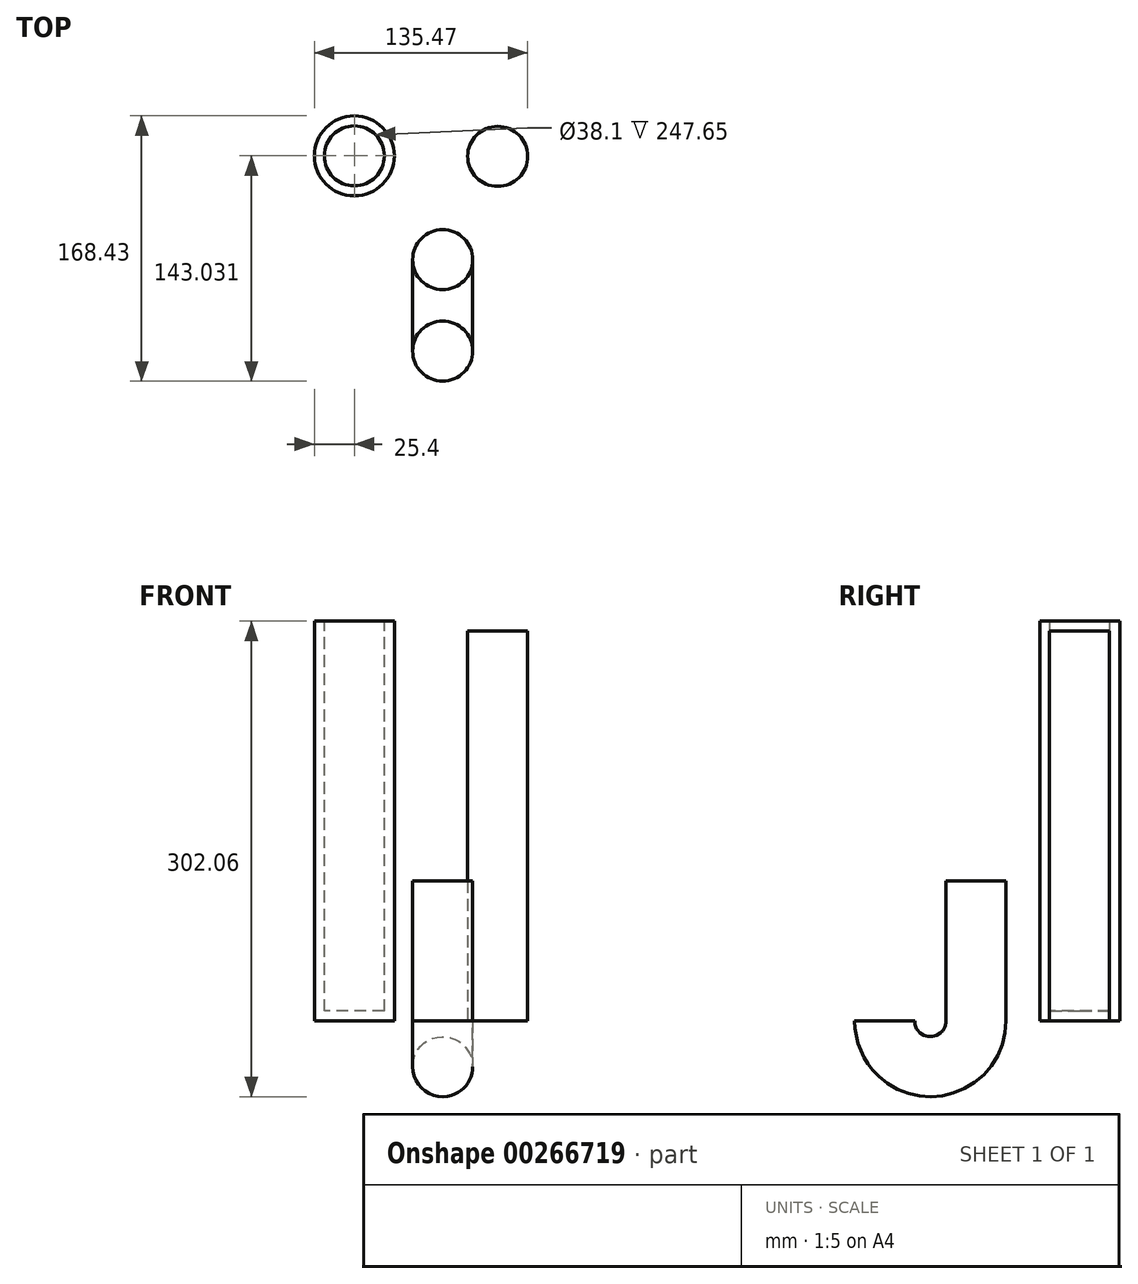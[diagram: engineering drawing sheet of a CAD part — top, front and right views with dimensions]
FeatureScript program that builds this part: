
annotation { "Feature Type Name" : "Feature", "Feature Type Description" : "" }
export const myFeature = defineFeature(function(context is Context, id is Id, definition is map)
    precondition{}
    {
        {
            var Q0;
            Q0=qCreatedBy(makeId("Top.planeOp"),FACE);
            var sketch = newSketch(context, id + "F0", { "sketchPlane" : qUnion([Q0])});
            skCircle(sketch, "E0", {"center": v(-56.08, 21.58) * mm, "radius": 25.4 * mm});
            skCircle(sketch, "E1", {"center": v(34.94, 21.29) * mm, "radius": 19.05 * mm});
            skCircle(sketch, "E2", {"center": v(0, -44.38) * mm, "radius": 19.05 * mm});
            skPoint(sketch, "E3.0", {"position": v(0, -102.4) * mm});
            skCircle(sketch, "E4", {"center": v(0, -102.4) * mm, "radius": 19.05 * mm});
            skSolve(sketch);
        }
        {
            var Q0;
            Q0=qCreatedBy(makeId("Right.planeOp"),FACE);
            var sketch = newSketch(context, id + "F1", { "sketchPlane" : qUnion([Q0])});
            skPoint(sketch, "E5.0", {"position": v(-44.38, 0) * mm});
            skArc(sketch, "E6", {"start": v(-102.4, 0) * mm, "mid": v(-73.4, -29) * mm, "end": v(-44.38, 0) * mm});
            skPoint(sketch, "E7", {"position": v(-102.4, 0) * mm});
            skSolve(sketch);
        }
        {
            var Q0;
            Q0=makeQuery(id+"F0.imprint","IMPRINT",FACE,{"disambiguationData":[TD([[makeQuery(id+"F0.imprint","IMPRINT",EDGE,{"derivedFrom":sQuery(id+"F0.wireOp",EDGE,"E0")}),1.0]])]});
            extrude(context, id + "F2", {"entities" : qUnion([Q0]), "depth" : 254 * mm});
        }
        {
            var Q0;
            Q0=makeQuery(id+"F0.imprint","IMPRINT",FACE,{"disambiguationData":[TD([[makeQuery(id+"F0.imprint","IMPRINT",EDGE,{"derivedFrom":sQuery(id+"F0.wireOp",EDGE,"E1")}),1.0]])]});
            extrude(context, id + "F3", {"entities" : qUnion([Q0]), "depth" : 247.65 * mm});
        }
        {
            var Q0;
            Q0=makeQuery(id+"F2.opExtrude","CAP_FACE",FACE,{"disambiguationData":[OSD([sQuery(id+"F0.wireOp",EDGE,"E0")])],"isStart":false});
            var sketch = newSketch(context, id + "F4", { "sketchPlane" : qUnion([Q0])});
            skCircle(sketch, "E8", {"center": v(-56.08, 21.58) * mm, "radius": 19.05 * mm});
            skSolve(sketch);
        }
        {
            var Q0;
            Q0=makeQuery(id+"F4.imprint","IMPRINT",FACE,{"disambiguationData":[TD([[makeQuery(id+"F4.imprint","IMPRINT",EDGE,{"derivedFrom":sQuery(id+"F4.wireOp",EDGE,"E8")}),1.0]])]});
            extrude(context, id + "F5", {"entities" : qUnion([Q0]), "operationType" : NewBodyOperationType.REMOVE, "oppositeDirection" : true, "depth" : 247.65 * mm});
        }
        {
            var Q0;
            Q0=makeQuery(id+"F0.imprint","IMPRINT",FACE,{"disambiguationData":[TD([[makeQuery(id+"F0.imprint","IMPRINT",EDGE,{"derivedFrom":sQuery(id+"F0.wireOp",EDGE,"E2")}),1.0]])]});
            extrude(context, id + "F6", {"entities" : qUnion([Q0]), "depth" : 88.9 * mm});
        }
        {
            var Q0;
            Q0=makeQuery(id+"F0.imprint","IMPRINT",FACE,{"disambiguationData":[TD([[makeQuery(id+"F0.imprint","IMPRINT",EDGE,{"derivedFrom":sQuery(id+"F0.wireOp",EDGE,"E4")}),1.0]])]});
            var Q1;
            Q1=sQuery(id+"F1.wireOp",EDGE,"E6");
            sweep(context, id + "F7", {"operationType" : NewBodyOperationType.ADD, "profiles" : qUnion([Q0]), "path" : qUnion([Q1])});
        }
    });
